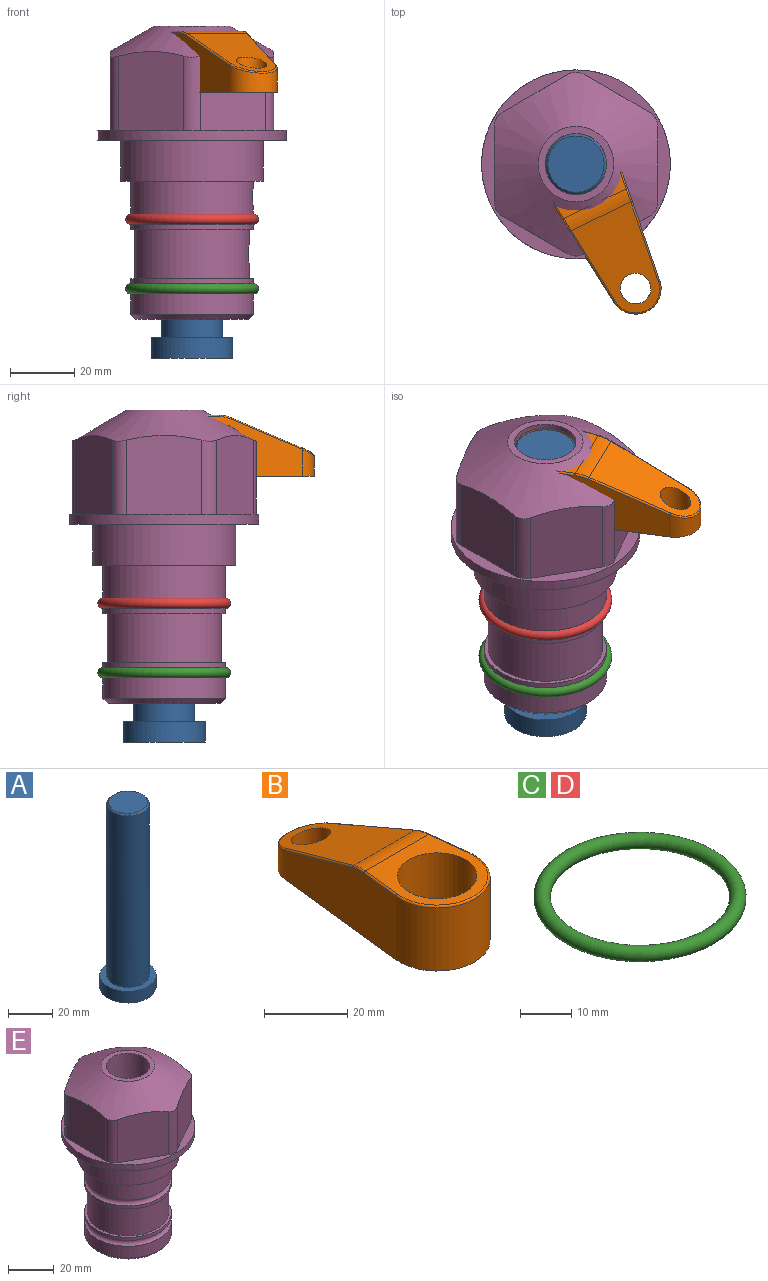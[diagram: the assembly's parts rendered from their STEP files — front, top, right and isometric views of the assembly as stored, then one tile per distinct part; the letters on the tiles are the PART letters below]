
ASSEMBLY  parts=5 mates=3
PART A: 6 faces, bbox 25.4x25.4x101.6 mm
  f0: plane 17.46x17.46mm, normal (0,0,1), area 239.5mm2, adj f5
  f1: plane 25.4x25.4mm, normal (0,0,-1), area 506.7mm2, adj f2
  f2: cylinder r=12.7mm len=25.4mm, axis (0,0,1), area 506.7mm2, adj f1,f3
  f3: plane 25.4x25.4mm, normal (0,0,1), area 221.7mm2, adj f2,f4
  f4: cylinder r=9.53mm len=94.46mm, axis (0,0,1), area 5653mm2, adj f3,f5
  f5: cone r=8.73mm half-angle=45deg, axis (0,0,-1), area 64.4mm2, adj f0,f4
PART B: 44 faces, bbox 27.5x64.5x19.1 mm
  f0: plane 2.3x0.95mm, normal (0,0,-1), area 1mm2, adj f25,f30,f34
  f1: plane 63.5x25.4mm, normal (0,0,-1), area 561.7mm2, adj f2,f3,f4,f5,f6,f7,f19,f20
  f2: cylinder r=12.7mm len=25.4mm, axis (0,0,-1), area 792.2mm2, adj f1,f3,f5,f13
  f3: plane 42.33x18.54mm, normal (0.99,0.11,0), area 647mm2, adj f1,f2,f4,f11,f12,f14
  f4: cylinder r=7.94mm len=15.78mm, axis (0,0,-1), area 158.6mm2, adj f1,f3,f5,f16
  f5: plane 42.33x18.54mm, normal (-0.99,0.11,0), area 647mm2, adj f1,f2,f4,f15,f17,f18
  f6: cylinder r=9.53mm len=19.05mm, axis (0,0,-1), area 1140.1mm2, adj f1,f8
  f7: cylinder r=4.76mm len=10.98mm, axis (0,0,-1), area 276.1mm2, adj f1,f9
  f8: plane 25.83x24.38mm, normal (0,0,1), area 262.2mm2, adj f6,f10,f11,f13,f15
  f9: plane 32.49x20.55mm, normal (0,0.34,0.94), area 489.9mm2, adj f7,f10,f14,f16,f18
  f10: cylinder r=12.7mm len=21.49mm, axis (-1,0,0), area 93.2mm2, adj f8,f9,f12,f17
  f11: cylinder r=0.51mm len=12.34mm, axis (0.11,-0.99,0), area 9.9mm2, adj f3,f8,f12,f13
  f12: bspline ~7.62x1.64mm, area 3.5mm2, adj f3,f10,f11,f14
  f13: torus R=12.19mm, axis (0,0,1), area 33.6mm2, adj f2,f8,f11,f15
  f14: cylinder r=0.51mm len=26.01mm, axis (0.1,-0.93,0.34), area 21.6mm2, adj f3,f9,f12,f16
  f15: cylinder r=0.51mm len=12.34mm, axis (0.11,0.99,0), area 9.9mm2, adj f5,f8,f13,f17
  f16: bspline ~15.78x7.05mm, area 15.7mm2, adj f4,f9,f14,f18
  f17: bspline ~7.62x1.64mm, area 3.5mm2, adj f5,f10,f15,f18
  f18: cylinder r=0.51mm len=26.01mm, axis (0.1,0.93,-0.34), area 21.6mm2, adj f5,f9,f16,f17
  f19: plane 21.6x14.29mm, normal (-0.99,-0.11,0), area 242.6mm2, adj f1,f26,f28,f34,f36,f38
  f20: plane 21.6x14.29mm, normal (0.99,-0.11,0), area 242.6mm2, adj f1,f27,f29,f37,f39,f41
  f21: cylinder r=12.7mm len=14.29mm, axis (0,0,-1), area 173.2mm2, adj f1,f26,f27,f30,f31,f33
  f22: cylinder r=7.94mm len=7.63mm, axis (0,0,-1), area 53.8mm2, adj f1,f28,f29,f42
  f23: plane 2.3x0.95mm, normal (0,0,-1), area 1mm2, adj f25,f33,f37
  f24: plane 17.94x12.32mm, normal (0,-0.34,-0.94), area 191.2mm2, adj f25,f38,f41,f42
  f25: cylinder r=9.53mm len=12.93mm, axis (-1,0,0), area 37.5mm2, adj f0,f23,f24,f31,f36,f39
  f26: cylinder r=1.59mm len=14.29mm, axis (0,0,-1), area 49mm2, adj f1,f19,f21,f32
  f27: cylinder r=1.59mm len=14.29mm, axis (0,0,-1), area 49mm2, adj f1,f20,f21,f35
  f28: cylinder r=1.59mm len=7.28mm, axis (0,0,-1), area 22.1mm2, adj f1,f19,f22,f40
  f29: cylinder r=1.59mm len=7.28mm, axis (0,0,-1), area 22.1mm2, adj f1,f20,f22,f43
  f30: torus R=14.29mm, axis (0,0,1), area 5.8mm2, adj f0,f21,f31,f32
  f31: bspline ~11.06x2.73mm, area 20.8mm2, adj f21,f25,f30,f33
  f32: sphere r=1.59mm, area 5.4mm2, adj f26,f30,f34
  f33: torus R=14.29mm, axis (0,0,1), area 5.8mm2, adj f21,f23,f31,f35
  f34: cylinder r=1.59mm len=1.68mm, axis (-0.11,0.99,0), area 2.4mm2, adj f0,f19,f32,f36
  f35: sphere r=1.59mm, area 5.4mm2, adj f27,f33,f37
  f36: bspline ~5.82x2.33mm, area 7.7mm2, adj f19,f25,f34,f38
  f37: cylinder r=1.59mm len=1.68mm, axis (0.11,0.99,0), area 2.4mm2, adj f20,f23,f35,f39
  f38: cylinder r=1.59mm len=18.33mm, axis (0.1,-0.93,0.34), area 46.7mm2, adj f19,f24,f36,f40
  f39: bspline ~5.82x2.33mm, area 7.7mm2, adj f20,f25,f37,f41
  f40: sphere r=1.59mm, area 3.6mm2, adj f28,f38,f42
  f41: cylinder r=1.59mm len=18.33mm, axis (0.1,0.93,-0.34), area 46.7mm2, adj f20,f24,f39,f43
  f42: bspline ~8.31x1.84mm, area 15.3mm2, adj f22,f24,f40,f43
  f43: sphere r=1.59mm, area 3.6mm2, adj f29,f41,f42
PART C: 1 faces, bbox 44.7x44.7x3.2 mm
  f0: torus R=19.05mm, axis (0,0,1), area 1193.9mm2
PART D: same geometry as C
PART E: 36 faces, bbox 58.7x58.7x91.2 mm
  f0: cylinder r=17.78mm len=35.56mm, axis (0,0,1), area 1670.8mm2, adj f23,f24,f31
  f1: cylinder r=19.05mm len=38.1mm, axis (0,0,1), area 1191.9mm2, adj f26,f27,f30
  f2: plane 58.66x58.66mm, normal (0,0,-1), area 1150.6mm2, adj f3,f28
  f3: cylinder r=29.33mm len=58.66mm, axis (0,0,-1), area 585.1mm2, adj f2,f4
  f4: plane 58.66x58.66mm, normal (0,0,1), area 475.9mm2, adj f3,f5,f6,f7,f8,f9,f10,f11
  f5: plane 24.5x20.32mm, normal (-0.5,0.87,0), area 562.8mm2, adj f4,f15,f16,f17
  f6: plane 24.5x20.32mm, normal (0.5,0.87,0), area 562.8mm2, adj f4,f14,f15,f17
  f7: plane 24.5x23.48mm, normal (1,0,0), area 562.8mm2, adj f4,f13,f14,f17
  f8: plane 24.5x20.32mm, normal (0.5,-0.87,0), area 562.8mm2, adj f4,f12,f13,f17
  f9: plane 24.5x20.32mm, normal (-0.5,-0.87,0), area 562.8mm2, adj f4,f11,f12,f17
  f10: plane 24.5x23.48mm, normal (-1,0,0), area 562.8mm2, adj f4,f11,f16,f17
  f11: cylinder r=5.08mm len=23.01mm, axis (0,0,-1), area 121.2mm2, adj f4,f9,f10,f17
  f12: cylinder r=5.08mm len=23.01mm, axis (0,0,-1), area 121.2mm2, adj f4,f8,f9,f17
  f13: cylinder r=5.08mm len=23.01mm, axis (0,0,-1), area 121.2mm2, adj f4,f7,f8,f17
  f14: cylinder r=5.08mm len=23.01mm, axis (0,0,-1), area 121.2mm2, adj f4,f6,f7,f17
  f15: cylinder r=5.08mm len=23.01mm, axis (0,0,-1), area 121.2mm2, adj f4,f5,f6,f17
  f16: cylinder r=5.08mm len=23.01mm, axis (0,0,-1), area 121.2mm2, adj f4,f5,f10,f17
  f17: cone r=11.73mm half-angle=60deg, axis (0,0,-1), area 2071.8mm2, adj f5,f6,f7,f8,f9,f10,f11,f12
  f18: plane 23.46x23.46mm, normal (0,0,1), area 147.4mm2, adj f17,f35
  f19: plane 34.93x34.93mm, normal (0,0,-1), area 958mm2, adj f29
  f20: cylinder r=19.05mm len=38.1mm, axis (0,0,1), area 760.1mm2, adj f21,f29
  f21: torus R=19.05mm, axis (0,0,1), area 565.3mm2, adj f20,f22
  f22: cylinder r=19.05mm len=38.1mm, axis (0,0,1), area 190mm2, adj f21,f23
  f23: plane 38.1x38.1mm, normal (0,0,1), area 146.9mm2, adj f0,f22
  f24: plane 38.1x38.1mm, normal (0,0,-1), area 146.9mm2, adj f0,f25
  f25: cylinder r=19.05mm len=38.1mm, axis (0,0,1), area 190mm2, adj f24,f26
  f26: torus R=19.05mm, axis (0,0,1), area 565.3mm2, adj f1,f25
  f27: plane 44.45x44.45mm, normal (0,0,-1), area 411.7mm2, adj f1,f28
  f28: cylinder r=22.23mm len=44.45mm, axis (0,0,1), area 1773.5mm2, adj f2,f27
  f29: cone r=19.05mm half-angle=45deg, axis (0,0,1), area 257.5mm2, adj f19,f20
  f30: cylinder r=3.17mm len=6.75mm, axis (-1,0,0), area 128mm2, adj f1,f33
  f31: cylinder r=3.17mm len=6.35mm, axis (-1,0,0), area 102.5mm2, adj f0,f33
  f32: plane 25.4x25.4mm, normal (0,0,1), area 506.7mm2, adj f33
  f33: cylinder r=12.7mm len=66.42mm, axis (0,0,-1), area 5236.2mm2, adj f30,f31,f32,f34
  f34: cone r=9.53mm half-angle=30deg, axis (0,0,-1), area 443.4mm2, adj f33,f35
  f35: cylinder r=9.53mm len=19.05mm, axis (0,0,-1), area 849mm2, adj f18,f34
PLACE A rot(axis=(0,0,-1),64.4deg) t=(0,0,-39.68)mm
PLACE B rot(axis=(0,0,-1),154.4deg) t=(0,0,14.93)mm
PLACE C t=(0,0,-21.59)mm
PLACE D at identity
PLACE E at identity fixed
MATE fastened C.f0 <-> E.f0  axis (0,0,1) through (0,0,-46.1)mm
MATE cylindrical A.f2 <-> E.f0  axis (0,0,1) through (0,0,-14.04)mm
MATE fastened B.f2 <-> A.f2  axis (0,0,1) through (0,0,33.98)mm
